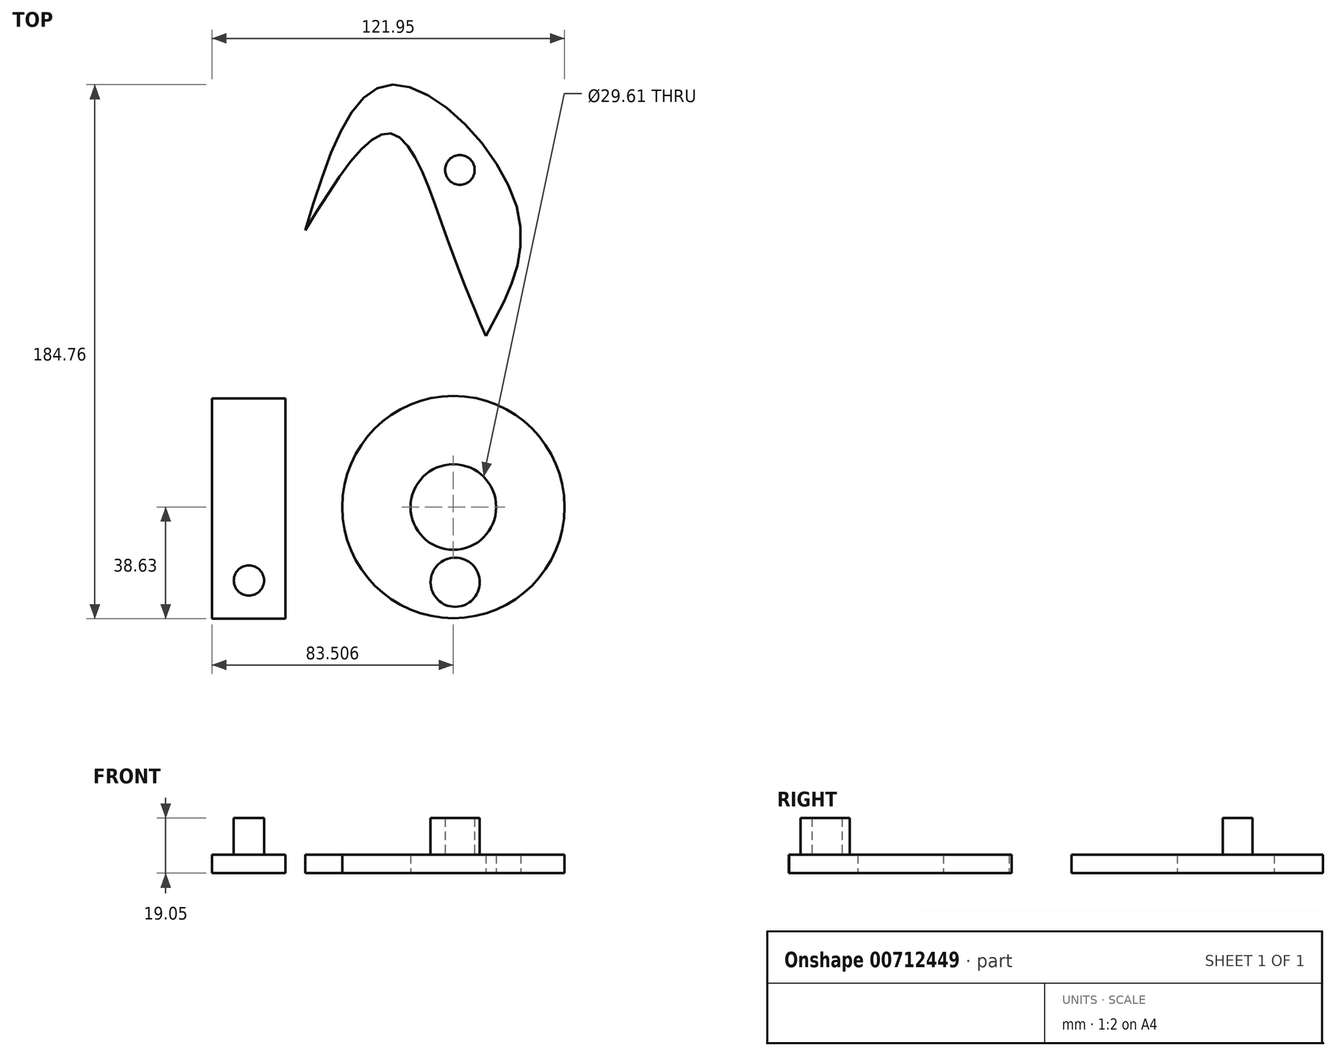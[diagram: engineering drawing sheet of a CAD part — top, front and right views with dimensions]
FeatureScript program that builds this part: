
annotation { "Feature Type Name" : "Feature", "Feature Type Description" : "" }
export const myFeature = defineFeature(function(context is Context, id is Id, definition is map)
    precondition{}
    {
        {
            var Q0;
            Q0=qCreatedBy(makeId("Top.planeOp"),FACE);
            var sketch = newSketch(context, id + "F0", { "sketchPlane" : qUnion([Q0])});
            skLineSegment(sketch, "E0.bottom", {"start": v(-61.98, 37.57) * mm, "end": v(-36.58, 37.57) * mm});
            skLineSegment(sketch, "E0.top", {"start": v(-61.98, -38.63) * mm, "end": v(-36.58, -38.63) * mm});
            skLineSegment(sketch, "E0.left", {"start": v(-61.98, 37.57) * mm, "end": v(-61.98, -38.63) * mm});
            skLineSegment(sketch, "E0.right", {"start": v(-36.58, 37.57) * mm, "end": v(-36.58, -38.63) * mm});
            skCircle(sketch, "E1", {"center": v(21.53, 0) * mm, "radius": 38.44 * mm});
            skCircle(sketch, "E2", {"center": v(21.53, 0) * mm, "radius": 14.8 * mm});
            skFitSpline(sketch, "E3", {"points": [v(32.71, 59.15) * mm, v(43.26, 104.33) * mm, v(0, 146.1) * mm, v(-29.72, 95.71) * mm], "startDerivative": vector(76.45, 137.53) * mm, "endDerivative": vector(-65.1, -215.17) * mm});
            skFitSpline(sketch, "E4", {"points": [v(-29.72, 95.71) * mm, v(0, 129.2) * mm, v(18.38, 95.71) * mm, v(32.71, 59.15) * mm], "startDerivative": vector(91.86, 150.34) * mm, "endDerivative": vector(42.02, -101) * mm});
            skSolve(sketch);
        }
        {
            var Q0;
            Q0 = qSketchRegion(id + "F0", true);
            extrude(context, id + "F1", {"entities" : qUnion([Q0]), "depth" : 6.35 * mm, "offsetDistance" : 25.4 * mm});
        }
        {
            var Q0;
            Q0=makeQuery(id+"F1.opExtrude","CAP_FACE",FACE,{"disambiguationData":[OSD([sQuery(id+"F0.wireOp",EDGE,"E0.bottom"),sQuery(id+"F0.wireOp",EDGE,"E0.top"),sQuery(id+"F0.wireOp",EDGE,"E0.left"),sQuery(id+"F0.wireOp",EDGE,"E0.right")])],"isStart":false});
            var sketch = newSketch(context, id + "F2", { "sketchPlane" : qUnion([Q0])});
            skCircle(sketch, "E5", {"center": v(-49.2, -25.41) * mm, "radius": 5.23 * mm});
            skCircle(sketch, "E6", {"center": v(22.14, -26.02) * mm, "radius": 8.51 * mm});
            skCircle(sketch, "E7", {"center": v(23.76, 116.63) * mm, "radius": 5.12 * mm});
            skSolve(sketch);
        }
        {
            var Q0;
            Q0 = qSketchRegion(id + "F2", true);
            extrude(context, id + "F3", {"entities" : qUnion([Q0]), "operationType" : NewBodyOperationType.ADD, "depth" : 12.7 * mm, "offsetDistance" : 25.4 * mm});
        }
    });
